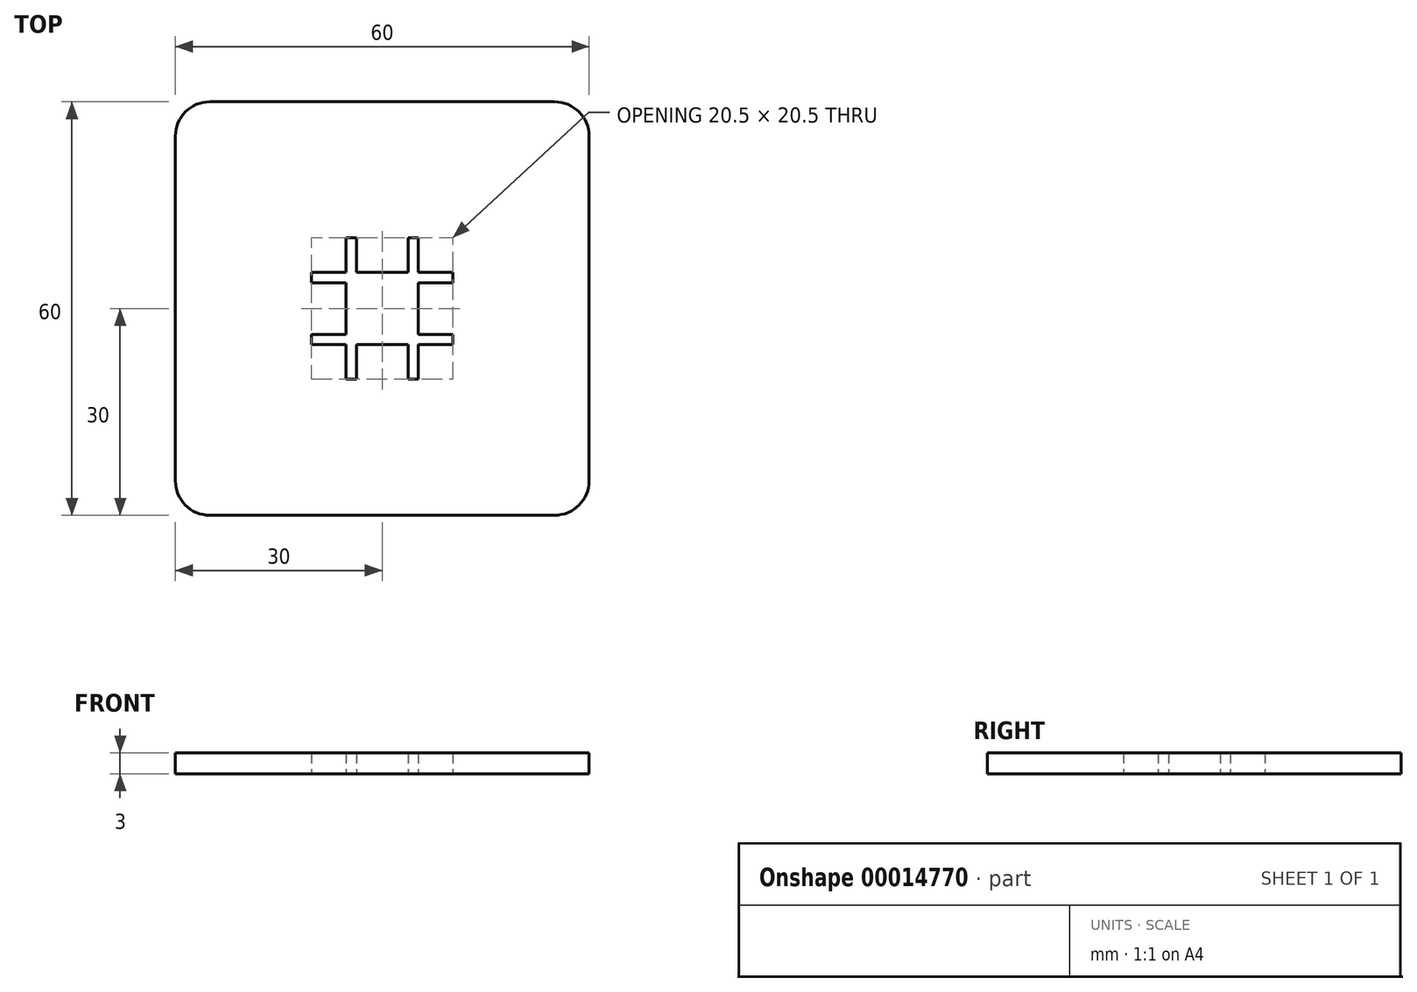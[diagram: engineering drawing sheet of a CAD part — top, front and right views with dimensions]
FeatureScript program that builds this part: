
annotation { "Feature Type Name" : "Feature", "Feature Type Description" : "" }
export const myFeature = defineFeature(function(context is Context, id is Id, definition is map)
    precondition{}
    {
        {
            var Q0;
            Q0=qCreatedBy(makeId("Top.planeOp"),FACE);
            var sketch = newSketch(context, id + "F0", { "sketchPlane" : qUnion([Q0])});
            skLineSegment(sketch, "E0.bottom", {"start": v(-25, 30) * mm, "end": v(25, 30) * mm});
            skLineSegment(sketch, "E0.top", {"start": v(-25, -30) * mm, "end": v(25, -30) * mm});
            skLineSegment(sketch, "E0.left", {"start": v(-30, 25) * mm, "end": v(-30, -25) * mm});
            skLineSegment(sketch, "E0.right", {"start": v(30, 25) * mm, "end": v(30, -25) * mm});
            skLineSegment(sketch, "E1.bottom", {"start": v(-9.92, 5.25) * mm, "end": v(-5.25, 5.25) * mm});
            skLineSegment(sketch, "E1.left", {"start": v(-5.25, 5.25) * mm, "end": v(-5.25, 10.25) * mm});
            skLineSegment(sketch, "E2.bottom", {"start": v(-5.25, 10.25) * mm, "end": v(-3.75, 10.25) * mm});
            skLineSegment(sketch, "E2.top", {"start": v(-5.25, 10.25) * mm, "end": v(-3.75, 10.25) * mm});
            skLineSegment(sketch, "E2.left", {"start": v(-5.25, 10.25) * mm, "end": v(-5.25, 10.25) * mm});
            skLineSegment(sketch, "E2.right", {"start": v(-3.75, 10.25) * mm, "end": v(-3.75, 10.25) * mm});
            skLineSegment(sketch, "E3", {"start": v(-3.75, 10.25) * mm, "end": v(-3.75, 5.25) * mm});
            skLineSegment(sketch, "E4", {"start": v(-3.75, 5.25) * mm, "end": v(3.75, 5.25) * mm});
            skLineSegment(sketch, "E5", {"start": v(3.75, 5.25) * mm, "end": v(3.75, 10.25) * mm});
            skLineSegment(sketch, "E6", {"start": v(3.75, 10.25) * mm, "end": v(5.25, 10.25) * mm});
            skLineSegment(sketch, "E7", {"start": v(5.25, 10.25) * mm, "end": v(5.25, 5.25) * mm});
            skLineSegment(sketch, "E8", {"start": v(5.25, 5.25) * mm, "end": v(10.25, 5.25) * mm});
            skLineSegment(sketch, "E9", {"start": v(10.25, 5.25) * mm, "end": v(10.25, 3.75) * mm});
            skLineSegment(sketch, "E10", {"start": v(10.25, 3.75) * mm, "end": v(5.25, 3.75) * mm});
            skLineSegment(sketch, "E11", {"start": v(5.25, 3.75) * mm, "end": v(5.25, 0) * mm});
            skLineSegment(sketch, "E12", {"start": v(-5.25, 5.25) * mm, "end": v(-10.25, 5.25) * mm});
            skLineSegment(sketch, "E13", {"start": v(-10.25, 5.25) * mm, "end": v(-10.25, 3.75) * mm});
            skLineSegment(sketch, "E14", {"start": v(-10.25, 3.75) * mm, "end": v(-5.25, 3.75) * mm});
            skLineSegment(sketch, "E15", {"start": v(-5.25, 3.75) * mm, "end": v(-5.25, 0) * mm});
            skLineSegment(sketch, "E16.MirrorCS", {"start": v(-5.25, -10.25) * mm, "end": v(-3.75, -10.25) * mm});
            skLineSegment(sketch, "E17.MirrorCS", {"start": v(-9.92, -5.25) * mm, "end": v(-5.25, -5.25) * mm});
            skLineSegment(sketch, "E18.MirrorCS", {"start": v(-10.25, -3.75) * mm, "end": v(-5.25, -3.75) * mm});
            skLineSegment(sketch, "E19.MirrorCS", {"start": v(3.75, -10.25) * mm, "end": v(5.25, -10.25) * mm});
            skLineSegment(sketch, "E20.MirrorCS", {"start": v(3.75, -5.25) * mm, "end": v(3.75, -10.25) * mm});
            skLineSegment(sketch, "E21.MirrorCS", {"start": v(-3.75, -5.25) * mm, "end": v(3.75, -5.25) * mm});
            skLineSegment(sketch, "E22.MirrorCS", {"start": v(-3.75, -10.25) * mm, "end": v(-3.75, -5.25) * mm});
            skLineSegment(sketch, "E23.MirrorCS", {"start": v(10.25, -3.75) * mm, "end": v(5.25, -3.75) * mm});
            skLineSegment(sketch, "E24.MirrorCS", {"start": v(-3.75, -10.25) * mm, "end": v(-3.75, -10.25) * mm});
            skLineSegment(sketch, "E25.MirrorCS", {"start": v(-5.25, -5.25) * mm, "end": v(-10.25, -5.25) * mm});
            skLineSegment(sketch, "E26.MirrorCS", {"start": v(5.25, -10.25) * mm, "end": v(5.25, -5.25) * mm});
            skLineSegment(sketch, "E27.MirrorCS", {"start": v(5.25, -3.75) * mm, "end": v(5.25, 0) * mm});
            skLineSegment(sketch, "E28.MirrorCS", {"start": v(10.25, -5.25) * mm, "end": v(10.25, -3.75) * mm});
            skLineSegment(sketch, "E29.MirrorCS", {"start": v(-5.25, -5.25) * mm, "end": v(-5.25, -10.25) * mm});
            skLineSegment(sketch, "E30.MirrorCS", {"start": v(5.25, -5.25) * mm, "end": v(10.25, -5.25) * mm});
            skLineSegment(sketch, "E31.MirrorCS", {"start": v(-5.25, -3.75) * mm, "end": v(-5.25, 0) * mm});
            skLineSegment(sketch, "E32.MirrorCS", {"start": v(-10.25, -5.25) * mm, "end": v(-10.25, -3.75) * mm});
            skLineSegment(sketch, "E33.MirrorCS", {"start": v(-5.25, -10.25) * mm, "end": v(-5.25, -10.25) * mm});
            skPoint(sketch, "E34.visualSharp", {"position": v(-30, 30) * mm});
            skArc(sketch, "E34.filletArc", {"start": v(-25, 30) * mm, "mid": v(-28.54, 28.54) * mm, "end": v(-30, 25) * mm});
            skPoint(sketch, "E35.visualSharp", {"position": v(30, 30) * mm});
            skArc(sketch, "E35.filletArc", {"start": v(30, 25) * mm, "mid": v(28.54, 28.54) * mm, "end": v(25, 30) * mm});
            skPoint(sketch, "E36.visualSharp", {"position": v(30, -30) * mm});
            skArc(sketch, "E36.filletArc", {"start": v(25, -30) * mm, "mid": v(28.54, -28.54) * mm, "end": v(30, -25) * mm});
            skPoint(sketch, "E37.visualSharp", {"position": v(-30, -30) * mm});
            skArc(sketch, "E37.filletArc", {"start": v(-30, -25) * mm, "mid": v(-28.54, -28.54) * mm, "end": v(-25, -30) * mm});
            skSolve(sketch);
        }
        {
            var Q0;
            Q0=makeQuery(id+"F0.imprint","IMPRINT",FACE,{"disambiguationData":[TD([[makeQuery(id+"F0.imprint","IMPRINT",EDGE,{"derivedFrom":sQuery(id+"F0.wireOp",EDGE,"E0.bottom")}),-1.0]])]});
            extrude(context, id + "F1", {"entities" : qUnion([Q0]), "depth" : 3 * mm});
        }
    });
